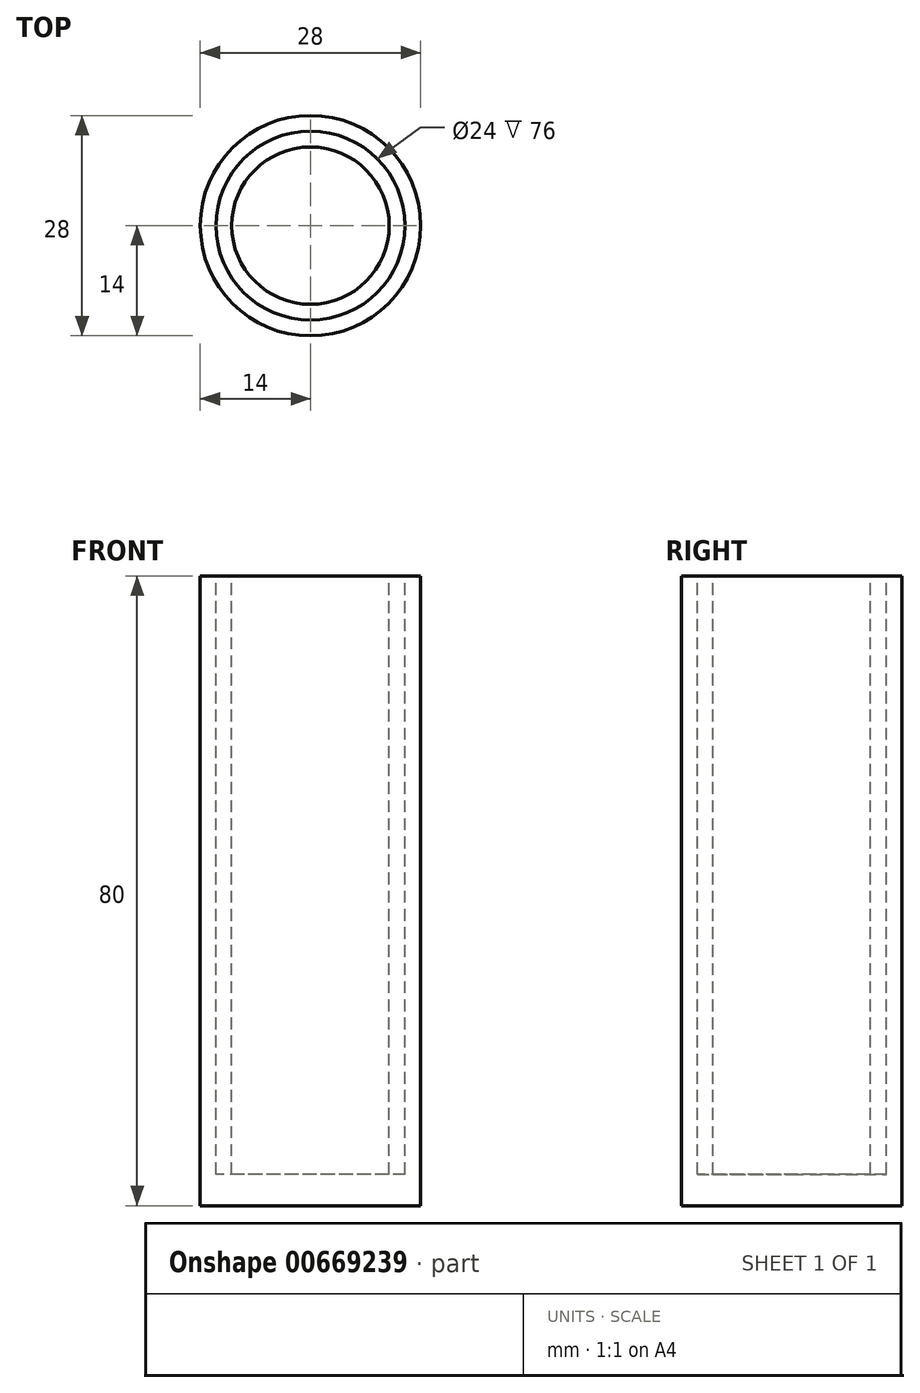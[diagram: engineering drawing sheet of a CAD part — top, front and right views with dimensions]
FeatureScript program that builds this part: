
annotation { "Feature Type Name" : "Feature", "Feature Type Description" : "" }
export const myFeature = defineFeature(function(context is Context, id is Id, definition is map)
    precondition{}
    {
        {
            var Q0;
            Q0=qCreatedBy(makeId("Front.planeOp"),FACE);
            var sketch = newSketch(context, id + "F0", { "sketchPlane" : qUnion([Q0])});
            skLineSegment(sketch, "E0", {"start": v(0, 0) * mm, "end": v(0, 453) * mm, "construction": true});
            skLineSegment(sketch, "E1", {"start": v(0, 0) * mm, "end": v(-14, 0) * mm});
            skLineSegment(sketch, "E2", {"start": v(-14, 0) * mm, "end": v(-14, 80) * mm});
            skLineSegment(sketch, "E3", {"start": v(-14, 80) * mm, "end": v(-12, 80) * mm});
            skLineSegment(sketch, "E4", {"start": v(-12, 80) * mm, "end": v(-12, 4) * mm});
            skLineSegment(sketch, "E5", {"start": v(-12, 4) * mm, "end": v(-10, 4) * mm});
            skLineSegment(sketch, "E6", {"start": v(-10, 4) * mm, "end": v(-10, 80) * mm});
            skLineSegment(sketch, "E7", {"start": v(-10, 80) * mm, "end": v(0, 80) * mm});
            skLineSegment(sketch, "E8", {"start": v(0, 80) * mm, "end": v(0, 0) * mm});
            skSolve(sketch);
        }
        {
            var Q0;
            Q0 = qSketchRegion(id + "F0", true);
            var Q1;
            Q1=sQuery(id+"F0.wireOp",EDGE,"E8");
            revolve(context, id + "F1", {"entities" : qUnion([Q0]), "axis" : qUnion([Q1]), "revolveType" : RevolveType.FULL});
        }
    });
